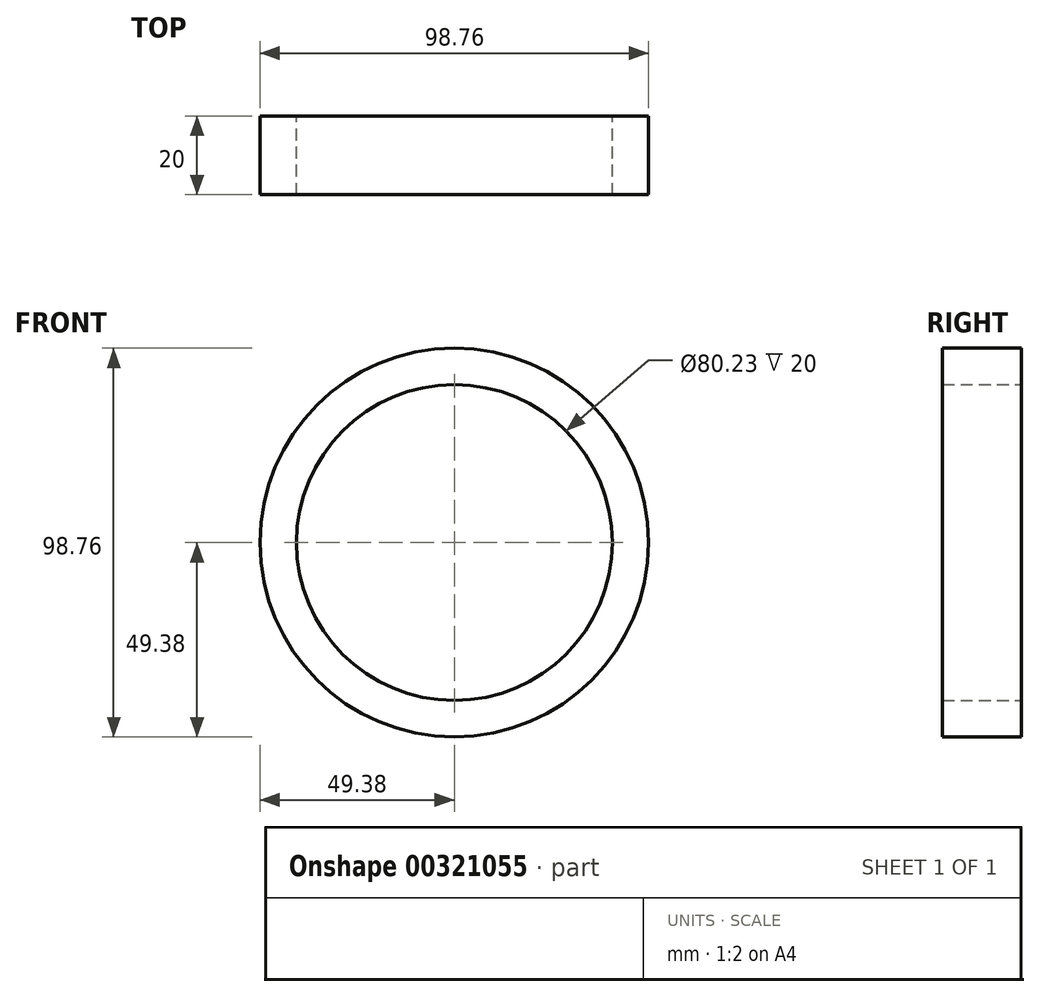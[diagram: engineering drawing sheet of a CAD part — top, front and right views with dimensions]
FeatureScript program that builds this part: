
annotation { "Feature Type Name" : "Feature", "Feature Type Description" : "" }
export const myFeature = defineFeature(function(context is Context, id is Id, definition is map)
    precondition{}
    {
        {
            var Q0;
            Q0=qCreatedBy(makeId("Front.planeOp"),FACE);
            var sketch = newSketch(context, id + "F0", { "sketchPlane" : qUnion([Q0])});
            skCircle(sketch, "E0", {"center": v(0, 0) * mm, "radius": 49.38 * mm});
            skCircle(sketch, "E1", {"center": v(0, 0) * mm, "radius": 40.12 * mm});
            skSolve(sketch);
        }
        {
            var Q0;
            Q0 = qSketchRegion(id + "F0", true);
            extrude(context, id + "F1", {"entities" : qUnion([Q0]), "depth" : 20 * mm});
        }
    });
